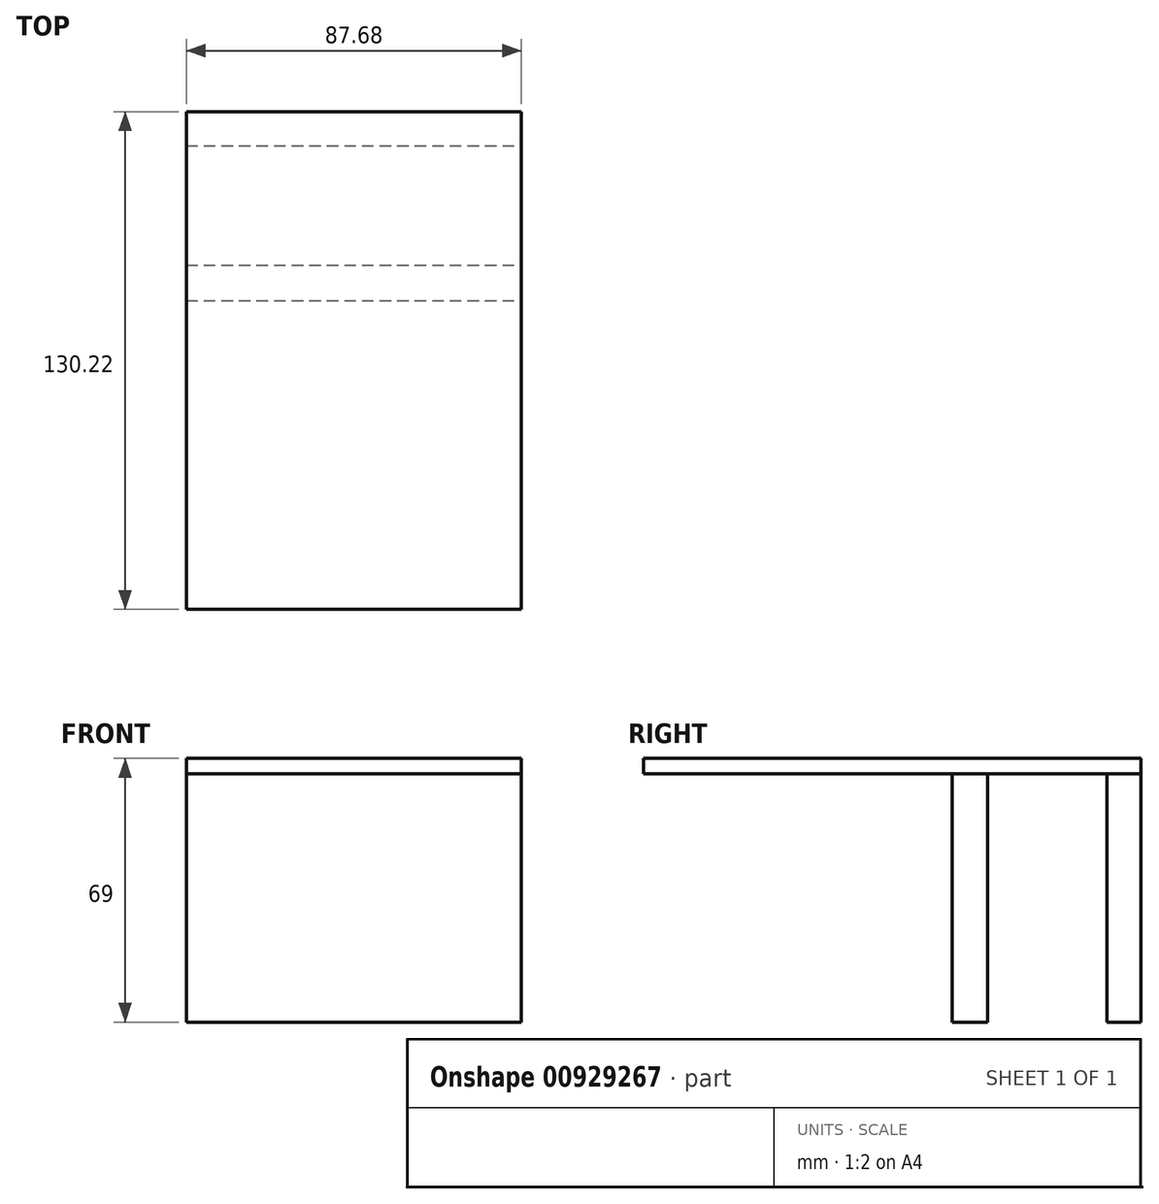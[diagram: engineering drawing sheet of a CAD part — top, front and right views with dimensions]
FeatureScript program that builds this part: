
annotation { "Feature Type Name" : "Feature", "Feature Type Description" : "" }
export const myFeature = defineFeature(function(context is Context, id is Id, definition is map)
    precondition{}
    {
        {
            var Q0;
            Q0=qCreatedBy(makeId("Top.planeOp"),FACE);
            var sketch = newSketch(context, id + "F0", { "sketchPlane" : qUnion([Q0])});
            skLineSegment(sketch, "E0.bottom", {"start": v(43.84, -65.11) * mm, "end": v(-43.84, -65.11) * mm});
            skLineSegment(sketch, "E0.top", {"start": v(43.84, 65.11) * mm, "end": v(-43.84, 65.11) * mm});
            skLineSegment(sketch, "E0.left", {"start": v(43.84, -65.11) * mm, "end": v(43.84, 65.11) * mm});
            skLineSegment(sketch, "E0.right", {"start": v(-43.84, -65.11) * mm, "end": v(-43.84, 65.11) * mm});
            skPoint(sketch, "E0.middle", {"position": v(0, 0) * mm});
            skLineSegment(sketch, "E1.bottom", {"start": v(-43.84, 65.11) * mm, "end": v(43.84, 65.11) * mm});
            skLineSegment(sketch, "E1.top", {"start": v(-43.84, 56.2) * mm, "end": v(43.84, 56.2) * mm});
            skLineSegment(sketch, "E1.left", {"start": v(-43.84, 65.11) * mm, "end": v(-43.84, 56.2) * mm});
            skLineSegment(sketch, "E1.right", {"start": v(43.84, 65.11) * mm, "end": v(43.84, 56.2) * mm});
            skLineSegment(sketch, "E2.bottom", {"start": v(-43.84, 24.96) * mm, "end": v(43.84, 24.96) * mm});
            skLineSegment(sketch, "E2.top", {"start": v(-43.84, 15.72) * mm, "end": v(43.84, 15.72) * mm});
            skLineSegment(sketch, "E2.left", {"start": v(-43.84, 24.96) * mm, "end": v(-43.84, 15.72) * mm});
            skLineSegment(sketch, "E2.right", {"start": v(43.84, 24.96) * mm, "end": v(43.84, 15.72) * mm});
            skArc(sketch, "E3", {"start": v(43.84, -65.11) * mm, "mid": v(0, -50.88) * mm, "end": v(-43.84, -65.11) * mm});
            skArc(sketch, "E4", {"start": v(43.84, -58.53) * mm, "mid": v(0.05, -44.43) * mm, "end": v(-43.84, -58.24) * mm});
            skSolve(sketch);
        }
        {
            var Q0;
            {var subQ0=sQuery(id+"F0.wireOp",EDGE,"E3");Q0=makeQuery(id+"F0.imprint","IMPRINT",FACE,{"disambiguationData":[TD([[makeQuery(id+"F0.imprint","IMPRINT",EDGE,{"derivedFrom":subQ0}),-1.0]])]});}
            var Q1;
            Q1=makeQuery(id+"F0.imprint","IMPRINT",FACE,{"disambiguationData":[TD([[makeQuery(id+"F0.imprint","IMPRINT",EDGE,{"derivedFrom":sQuery(id+"F0.wireOp",EDGE,"E0.bottom")}),-1.0]])]});
            var Q2;
            {var subQ0=sQuery(id+"F0.wireOp",EDGE,"E1.top");Q2=makeQuery(id+"F0.imprint","IMPRINT",FACE,{"disambiguationData":[TD([[makeQuery(id+"F0.imprint","IMPRINT",EDGE,{"derivedFrom":subQ0}),-1.0]])]});}
            var Q3;
            {var subQ0=sQuery(id+"F0.wireOp",EDGE,"E0.top");Q3=makeQuery(id+"F0.imprint","IMPRINT",FACE,{"disambiguationData":[TD([[makeQuery(id+"F0.imprint","IMPRINT",EDGE,{"derivedFrom":subQ0}),1.0]])]});}
            var Q4;
            {var subQ3=sQuery(id+"F0.wireOp",EDGE,"E2.top");var subQ8=makeQuery(id+"F0.imprint","IMPRINT",EDGE,{"derivedFrom":subQ3});var subQ10=sQuery(id+"F0.wireOp",EDGE,"E3");var subQ11=sQuery(id+"F0.wireOp",EDGE,"E0.bottom");var subQ12=makeQuery(id+"F0.imprint","IMPRINT",EDGE,{"derivedFrom":subQ10});var subQ13=sQuery(id+"F0.wireOp",EDGE,"E0.top");var subQ14=sQuery(id+"F0.wireOp",EDGE,"E1.top");var subQ17=makeQuery(id+"F0.imprint","IMPRINT",EDGE,{"derivedFrom":subQ14});var subQ18=sQuery(id+"F0.wireOp",EDGE,"E2.bottom");var subQ21=makeQuery(id+"F0.imprint","IMPRINT",EDGE,{"derivedFrom":subQ18});Q4=qUnion([makeQuery(id+"F0.imprint","IMPRINT",FACE,{"disambiguationData":[TD([[subQ17,-1.0]])]}),makeQuery(id+"F0.imprint","IMPRINT",FACE,{"disambiguationData":[TD([[makeQuery(id+"F0.imprint","IMPRINT",EDGE,{"derivedFrom":subQ11}),-1.0]])]}),makeQuery(id+"F0.imprint","IMPRINT",FACE,{"disambiguationData":[TD([[subQ21,-1.0]])]}),makeQuery(id+"F0.imprint","IMPRINT",FACE,{"disambiguationData":[TD([[makeQuery(id+"F0.imprint","IMPRINT",EDGE,{"derivedFrom":subQ13}),1.0]])]}),makeQuery(id+"F0.imprint","IMPRINT",FACE,{"disambiguationData":[TD([[subQ12,-1.0]])]}),makeQuery(id+"F0.imprint","IMPRINT",FACE,{"disambiguationData":[TD([[subQ8,-1.0]])]})]);}
            var Q5;
            {var subQ0=sQuery(id+"F0.wireOp",EDGE,"E2.bottom");Q5=makeQuery(id+"F0.imprint","IMPRINT",FACE,{"disambiguationData":[TD([[makeQuery(id+"F0.imprint","IMPRINT",EDGE,{"derivedFrom":subQ0}),-1.0]])]});}
            var Q6;
            {var subQ2=sQuery(id+"F0.wireOp",EDGE,"E2.top");Q6=makeQuery(id+"F0.imprint","IMPRINT",FACE,{"disambiguationData":[TD([[makeQuery(id+"F0.imprint","IMPRINT",EDGE,{"derivedFrom":subQ2}),-1.0]])]});}
            extrude(context, id + "F1", {"entities" : qUnion([Q0, Q1, Q2, Q3, Q4, Q5, Q6]), "depth" : 4 * mm, "offsetDistance" : 25 * mm});
        }
        {
            var Q0;
            {var subQ0=sQuery(id+"F0.wireOp",EDGE,"E2.bottom");Q0=makeQuery(id+"F0.imprint","IMPRINT",FACE,{"disambiguationData":[TD([[makeQuery(id+"F0.imprint","IMPRINT",EDGE,{"derivedFrom":subQ0}),-1.0]])]});}
            var Q1;
            {var subQ0=sQuery(id+"F0.wireOp",EDGE,"E0.top");Q1=makeQuery(id+"F0.imprint","IMPRINT",FACE,{"disambiguationData":[TD([[makeQuery(id+"F0.imprint","IMPRINT",EDGE,{"derivedFrom":subQ0}),1.0]])]});}
            extrude(context, id + "F2", {"entities" : qUnion([Q0, Q1]), "oppositeDirection" : true, "depth" : 65 * mm, "offsetDistance" : 25 * mm});
        }
    });
